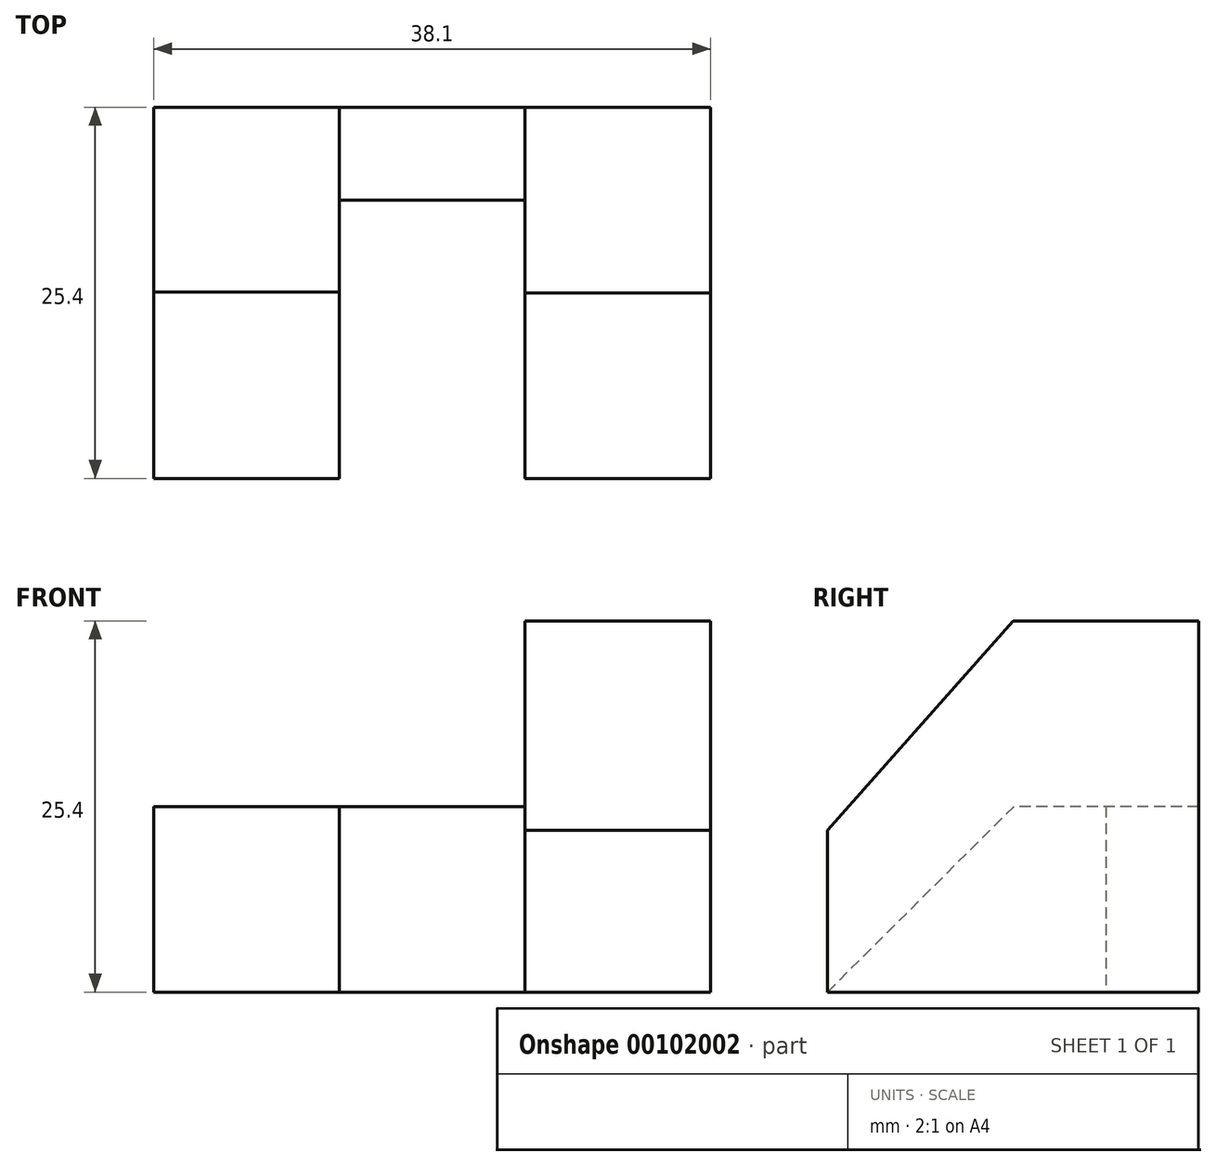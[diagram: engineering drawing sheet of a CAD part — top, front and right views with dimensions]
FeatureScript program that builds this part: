
annotation { "Feature Type Name" : "Feature", "Feature Type Description" : "" }
export const myFeature = defineFeature(function(context is Context, id is Id, definition is map)
    precondition{}
    {
        {
            var Q0;
            Q0=qCreatedBy(makeId("Right.planeOp"),FACE);
            var sketch = newSketch(context, id + "F0", { "sketchPlane" : qUnion([Q0])});
            skLineSegment(sketch, "E0", {"start": v(0, -1.64) * mm, "end": v(0, 11.06) * mm});
            skLineSegment(sketch, "E1", {"start": v(0, 11.06) * mm, "end": v(12.7, 25.4) * mm});
            skLineSegment(sketch, "E2", {"start": v(12.7, 25.4) * mm, "end": v(25.4, 25.4) * mm});
            skLineSegment(sketch, "E3", {"start": v(25.4, 25.4) * mm, "end": v(25.4, 0) * mm});
            skLineSegment(sketch, "E4", {"start": v(25.4, 0) * mm, "end": v(0, 0) * mm});
            skSolve(sketch);
        }
        {
            var Q0;
            Q0 = qSketchRegion(id + "F0", true);
            extrude(context, id + "F1", {"entities" : qUnion([Q0]), "depth" : 12.7 * mm});
        }
        {
            var Q0;
            Q0=qCreatedBy(makeId("Right.planeOp"),FACE);
            var sketch = newSketch(context, id + "F2", { "sketchPlane" : qUnion([Q0])});
            skLineSegment(sketch, "E5", {"start": v(25.4, 0) * mm, "end": v(25.4, 12.7) * mm});
            skLineSegment(sketch, "E6", {"start": v(25.4, 12.7) * mm, "end": v(12.76, 12.7) * mm});
            skLineSegment(sketch, "E7", {"start": v(12.76, 12.7) * mm, "end": v(0, 0) * mm});
            skLineSegment(sketch, "E8", {"start": v(0, 0) * mm, "end": v(25.4, 0) * mm});
            skSolve(sketch);
        }
        {
            var Q0;
            Q0 = qSketchRegion(id + "F2", true);
            extrude(context, id + "F3", {"entities" : qUnion([Q0]), "oppositeDirection" : true, "depth" : 25.4 * mm, "hasSecondDirection" : true, "secondDirectionOppositeDirection" : true, "secondDirectionDepth" : 12.7 * mm});
        }
        {
            var Q0;
            Q0=qCreatedBy(makeId("Front.planeOp"),FACE);
            var sketch = newSketch(context, id + "F4", { "sketchPlane" : qUnion([Q0])});
            skLineSegment(sketch, "E9", {"start": v(0, 0) * mm, "end": v(-12.7, 0) * mm});
            skLineSegment(sketch, "E10", {"start": v(-12.7, 0) * mm, "end": v(-12.7, 12.7) * mm});
            skLineSegment(sketch, "E11", {"start": v(-12.7, 12.7) * mm, "end": v(0, 12.7) * mm});
            skLineSegment(sketch, "E12", {"start": v(0, 12.7) * mm, "end": v(0, 0) * mm});
            skSolve(sketch);
        }
        {
            var Q0;
            Q0=makeQuery(id+"F4.imprint","IMPRINT",FACE,{"disambiguationData":[TD([[makeQuery(id+"F4.imprint","IMPRINT",EDGE,{"derivedFrom":sQuery(id+"F4.wireOp",EDGE,"E9")}),-1.0]])]});
            extrude(context, id + "F5", {"entities" : qUnion([Q0]), "oppositeDirection" : true, "depth" : 25.4 * mm, "hasSecondDirection" : true, "secondDirectionOppositeDirection" : true, "secondDirectionDepth" : 19.05 * mm});
        }
    });
